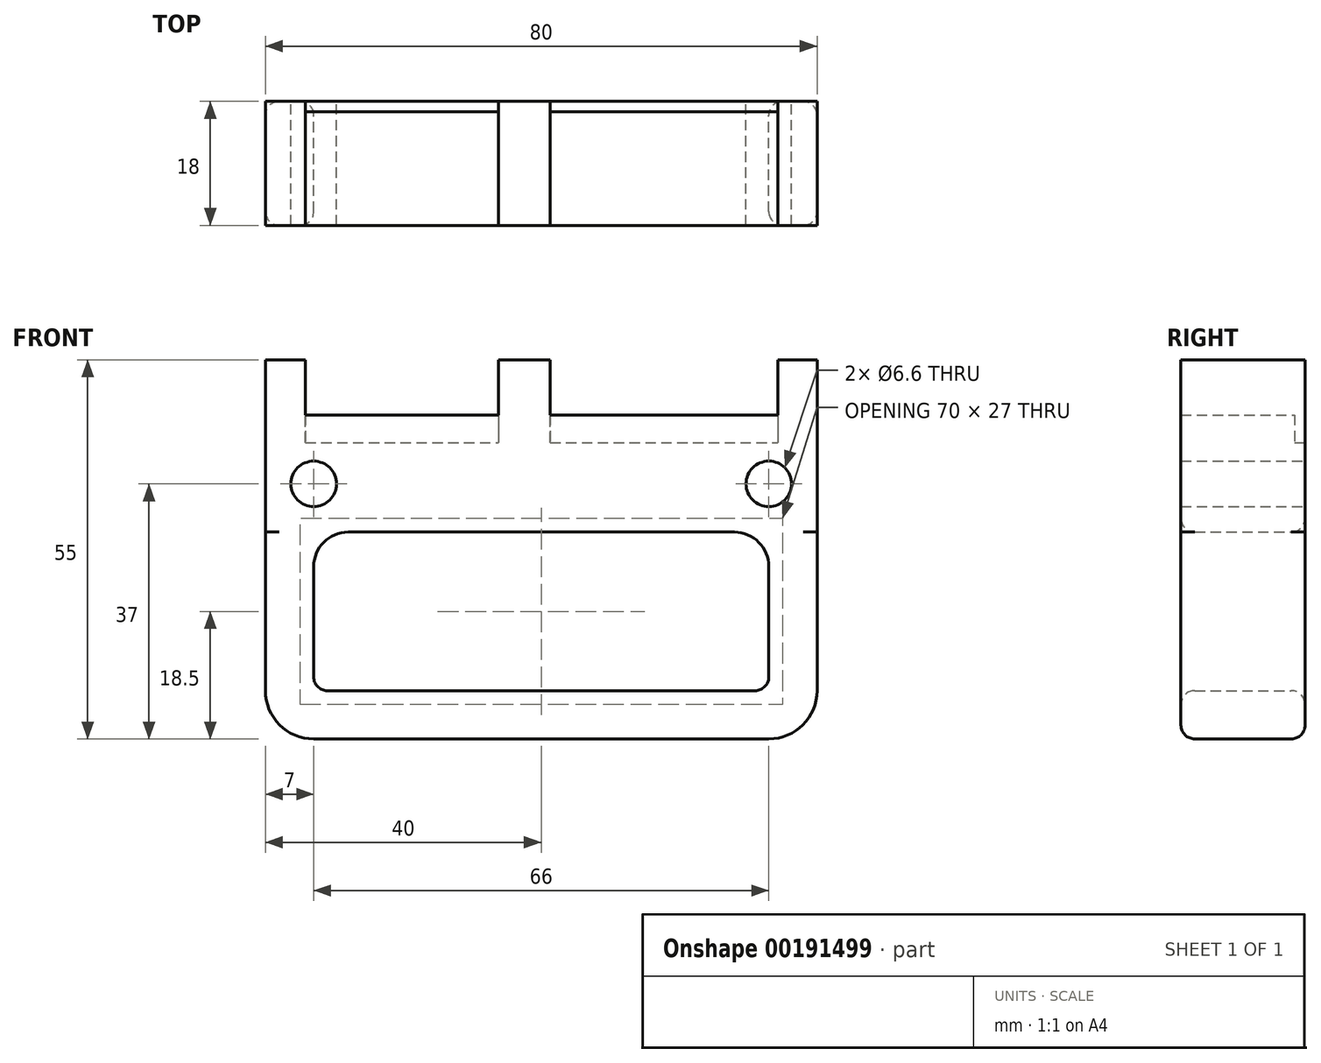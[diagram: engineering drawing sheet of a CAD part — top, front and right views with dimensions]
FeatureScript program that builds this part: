
annotation { "Feature Type Name" : "Feature", "Feature Type Description" : "" }
export const myFeature = defineFeature(function(context is Context, id is Id, definition is map)
    precondition{}
    {
        {
            var Q0;
            Q0=qCreatedBy(makeId("Front.planeOp"),FACE);
            var sketch = newSketch(context, id + "F0", { "sketchPlane" : qUnion([Q0])});
            skLineSegment(sketch, "E0.left", {"start": v(0, 0) * mm, "end": v(0, 25) * mm});
            skLineSegment(sketch, "E0.right", {"start": v(80, 0) * mm, "end": v(80, 25) * mm});
            skLineSegment(sketch, "E1", {"start": v(80, 25) * mm, "end": v(74.3, 25) * mm});
            skLineSegment(sketch, "E2", {"start": v(74.3, 25) * mm, "end": v(74.3, 17) * mm});
            skLineSegment(sketch, "E3", {"start": v(74.3, 17) * mm, "end": v(41.3, 17) * mm});
            skLineSegment(sketch, "E4", {"start": v(41.3, 17) * mm, "end": v(41.3, 25) * mm});
            skLineSegment(sketch, "E5", {"start": v(41.3, 25) * mm, "end": v(33.8, 25) * mm});
            skLineSegment(sketch, "E6", {"start": v(33.8, 25) * mm, "end": v(33.8, 17) * mm});
            skLineSegment(sketch, "E7", {"start": v(33.8, 17) * mm, "end": v(5.8, 17) * mm});
            skLineSegment(sketch, "E8", {"start": v(5.8, 17) * mm, "end": v(5.8, 25) * mm});
            skLineSegment(sketch, "E9", {"start": v(5.8, 25) * mm, "end": v(0, 25) * mm});
            skLineSegment(sketch, "E10.top", {"start": v(0, 7) * mm, "end": v(7, 7) * mm, "construction": true});
            skLineSegment(sketch, "E10.left", {"start": v(0, 0) * mm, "end": v(0, 7) * mm, "construction": true});
            skLineSegment(sketch, "E10.right", {"start": v(7, 0) * mm, "end": v(7, 7) * mm, "construction": true});
            skLineSegment(sketch, "E11.top", {"start": v(80, 7) * mm, "end": v(73, 7) * mm, "construction": true});
            skLineSegment(sketch, "E11.left", {"start": v(80, 0) * mm, "end": v(80, 7) * mm, "construction": true});
            skLineSegment(sketch, "E11.right", {"start": v(73, 0) * mm, "end": v(73, 7) * mm, "construction": true});
            skCircle(sketch, "E12", {"center": v(7, 7) * mm, "radius": 3.3 * mm});
            skCircle(sketch, "E13", {"center": v(73, 7) * mm, "radius": 3.3 * mm});
            skLineSegment(sketch, "E14.top", {"start": v(12, 0) * mm, "end": v(68, 0) * mm});
            skPoint(sketch, "E15.visualSharp", {"position": v(0, -30) * mm});
            skPoint(sketch, "E16.visualSharp", {"position": v(80, -30) * mm});
            skPoint(sketch, "E17.visualSharp", {"position": v(7, -23) * mm});
            skPoint(sketch, "E18.visualSharp", {"position": v(73, -23) * mm});
            skPoint(sketch, "E19.visualSharp", {"position": v(73, 0) * mm});
            skArc(sketch, "E19.filletArc", {"start": v(73, -5) * mm, "mid": v(71.54, -1.46) * mm, "end": v(68, 0) * mm});
            skPoint(sketch, "E20.visualSharp", {"position": v(7, 0) * mm});
            skArc(sketch, "E20.filletArc", {"start": v(12, 0) * mm, "mid": v(8.46, -1.46) * mm, "end": v(7, -5) * mm});
            skLineSegment(sketch, "E21", {"start": v(0, 0) * mm, "end": v(0, -23) * mm});
            skLineSegment(sketch, "E22", {"start": v(73, -30) * mm, "end": v(7, -30) * mm});
            skLineSegment(sketch, "E23", {"start": v(80, 0) * mm, "end": v(80, -23) * mm});
            skArc(sketch, "E24.filletArc", {"start": v(0, -23) * mm, "mid": v(2.05, -27.95) * mm, "end": v(7, -30) * mm});
            skArc(sketch, "E25.filletArc", {"start": v(73, -30) * mm, "mid": v(77.95, -27.95) * mm, "end": v(80, -23) * mm});
            skLineSegment(sketch, "E26.bottom", {"start": v(0, -30) * mm, "end": v(7, -30) * mm, "construction": true});
            skLineSegment(sketch, "E26.top", {"start": v(0, -23) * mm, "end": v(7, -23) * mm, "construction": true});
            skLineSegment(sketch, "E26.left", {"start": v(0, -30) * mm, "end": v(0, -23) * mm, "construction": true});
            skLineSegment(sketch, "E26.right", {"start": v(7, -30) * mm, "end": v(7, -23) * mm, "construction": true});
            skLineSegment(sketch, "E27.bottom", {"start": v(80, -30) * mm, "end": v(73, -30) * mm, "construction": true});
            skLineSegment(sketch, "E27.top", {"start": v(80, -23) * mm, "end": v(73, -23) * mm, "construction": true});
            skLineSegment(sketch, "E27.left", {"start": v(80, -30) * mm, "end": v(80, -23) * mm, "construction": true});
            skLineSegment(sketch, "E27.right", {"start": v(73, -30) * mm, "end": v(73, -23) * mm, "construction": true});
            skLineSegment(sketch, "E28", {"start": v(7, -5) * mm, "end": v(7, -21) * mm});
            skLineSegment(sketch, "E29", {"start": v(9, -23) * mm, "end": v(71, -23) * mm});
            skLineSegment(sketch, "E30", {"start": v(73, -5) * mm, "end": v(73, -21) * mm});
            skArc(sketch, "E31.filletArc", {"start": v(7, -21) * mm, "mid": v(7.59, -22.41) * mm, "end": v(9, -23) * mm});
            skArc(sketch, "E32.filletArc", {"start": v(71, -23) * mm, "mid": v(72.41, -22.41) * mm, "end": v(73, -21) * mm});
            skSolve(sketch);
        }
        {
            var Q0;
            Q0=makeQuery(id+"F0.imprint","IMPRINT",FACE,{"disambiguationData":[TD([[makeQuery(id+"F0.imprint","IMPRINT",EDGE,{"derivedFrom":sQuery(id+"F0.wireOp",EDGE,"E0.left")}),-1.0]])]});
            extrude(context, id + "F1", {"entities" : qUnion([Q0]), "depth" : 18 * mm});
        }
        {
            var Q0;
            Q0=makeQuery(id+"F1.opExtrude","CAP_FACE",FACE,{"disambiguationData":[OSD([sQuery(id+"F0.wireOp",EDGE,"E0.bottom"),sQuery(id+"F0.wireOp",EDGE,"E0.left"),sQuery(id+"F0.wireOp",EDGE,"E0.right"),sQuery(id+"F0.wireOp",EDGE,"E1"),sQuery(id+"F0.wireOp",EDGE,"E2"),sQuery(id+"F0.wireOp",EDGE,"E3"),sQuery(id+"F0.wireOp",EDGE,"E4"),sQuery(id+"F0.wireOp",EDGE,"E5"),sQuery(id+"F0.wireOp",EDGE,"E6"),sQuery(id+"F0.wireOp",EDGE,"E7"),sQuery(id+"F0.wireOp",EDGE,"E8"),sQuery(id+"F0.wireOp",EDGE,"E9"),sQuery(id+"F0.wireOp",EDGE,"E12"),sQuery(id+"F0.wireOp",EDGE,"E13"),sQuery(id+"F0.wireOp",EDGE,"ocKFlsXm-vWDa-OrpV-uGXT-8O8tEcb7mLHl.top"),sQuery(id+"F0.wireOp",EDGE,"ocKFlsXm-vWDa-OrpV-uGXT-8O8tEcb7mLHl.left"),sQuery(id+"F0.wireOp",EDGE,"ocKFlsXm-vWDa-OrpV-uGXT-8O8tEcb7mLHl.right"),sQuery(id+"F0.wireOp",EDGE,"41f4592c-d5e8-44ce-ae2d-2787e6d9c6fd.trimOffspring")])],"isStart":true});
            var sketch = newSketch(context, id + "F2", { "sketchPlane" : qUnion([Q0])});
            skLineSegment(sketch, "E33.left", {"start": v(-74.3, 17) * mm, "end": v(-74.3, 13) * mm});
            skLineSegment(sketch, "E34.left", {"start": v(-33.8, 17) * mm, "end": v(-33.8, 13) * mm});
            skLineSegment(sketch, "E35.left", {"start": v(-41.3, 17) * mm, "end": v(-41.3, 13) * mm});
            skLineSegment(sketch, "E36", {"start": v(-74.3, 17) * mm, "end": v(-41.3, 17) * mm});
            skLineSegment(sketch, "E37", {"start": v(-41.3, 13) * mm, "end": v(-74.3, 13) * mm});
            skLineSegment(sketch, "E38", {"start": v(-33.8, 17) * mm, "end": v(-5.8, 17) * mm});
            skLineSegment(sketch, "E39", {"start": v(-5.8, 17) * mm, "end": v(-5.8, 13) * mm});
            skLineSegment(sketch, "E40", {"start": v(-5.8, 13) * mm, "end": v(-33.8, 13) * mm});
            skSolve(sketch);
        }
        {
            var Q0;
            Q0 = qSketchRegion(id + "F2", true);
            extrude(context, id + "F3", {"entities" : qUnion([Q0]), "operationType" : NewBodyOperationType.REMOVE, "oppositeDirection" : true, "depth" : 1.5 * mm});
        }
        {
            var Q0;
            Q0=makeQuery(id+"F1.opExtrude","CAP_EDGE",EDGE,{"disambiguationData":[OSD([sQuery(id+"F0.wireOp",EDGE,"E32.filletArc")])],"isStart":true});
            var Q1;
            Q1=makeQuery(id+"F1.opExtrude","CAP_EDGE",EDGE,{"disambiguationData":[OSD([sQuery(id+"F0.wireOp",EDGE,"E30")])],"isStart":true});
            var Q2;
            Q2=makeQuery(id+"F1.opExtrude","CAP_EDGE",EDGE,{"disambiguationData":[OSD([sQuery(id+"F0.wireOp",EDGE,"E28")])],"isStart":false});
            var Q3;
            Q3=makeQuery(id+"F1.opExtrude","CAP_EDGE",EDGE,{"disambiguationData":[OSD([sQuery(id+"F0.wireOp",EDGE,"E22")])],"isStart":true});
            var Q4;
            Q4=makeQuery(id+"F1.opExtrude","CAP_EDGE",EDGE,{"disambiguationData":[OSD([sQuery(id+"F0.wireOp",EDGE,"E0.left"),sQuery(id+"F0.wireOp",EDGE,"E21")])],"isStart":false});
            fillet(context, id + "F4", {"entities" : qUnion([Q0, Q1, Q2, Q3, Q4]), "radius" : 2 * mm, "tangentPropagation" : true, "allowEdgeOverflow" : false});
        }
        {
            var Q0;
            Q0=makeQuery(id+"F1.opExtrude","SWEPT_FACE",FACE,{"disambiguationData":[OSD([sQuery(id+"F0.wireOp",EDGE,"E9")])]});
            var sketch = newSketch(context, id + "F5", { "sketchPlane" : qUnion([Q0])});
            skLineSegment(sketch, "E41.bottom", {"start": v(5.8, 0) * mm, "end": v(0, 0) * mm});
            skLineSegment(sketch, "E41.top", {"start": v(5.8, -18) * mm, "end": v(0, -18) * mm});
            skLineSegment(sketch, "E41.left", {"start": v(5.8, 0) * mm, "end": v(5.8, -18) * mm});
            skLineSegment(sketch, "E41.right", {"start": v(0, 0) * mm, "end": v(0, -18) * mm});
            skLineSegment(sketch, "E42", {"start": v(5.8, 0) * mm, "end": v(74.3, 0) * mm, "construction": true});
            skLineSegment(sketch, "E43.bottom", {"start": v(74.3, 0) * mm, "end": v(80, 0) * mm});
            skLineSegment(sketch, "E43.top", {"start": v(74.3, -18) * mm, "end": v(80, -18) * mm});
            skLineSegment(sketch, "E43.left", {"start": v(74.3, 0) * mm, "end": v(74.3, -18) * mm});
            skLineSegment(sketch, "E43.right", {"start": v(80, 0) * mm, "end": v(80, -18) * mm});
            skSolve(sketch);
        }
        {
            var Q0;
            Q0 = qSketchRegion(id + "F5", true);
            extrude(context, id + "F6", {"entities" : qUnion([Q0]), "operationType" : NewBodyOperationType.ADD, "oppositeDirection" : true, "depth" : 25 * mm});
        }
        {
            var Q0;
            Q0=makeQuery(id+"F6.boolean.opBoolean","MERGE",FACE,{"derivedFrom":[makeQuery(id+"F1.opExtrude","CAP_FACE",FACE,{"disambiguationData":[OSD([sQuery(id+"F0.wireOp",EDGE,"E0.left"),sQuery(id+"F0.wireOp",EDGE,"E0.right"),sQuery(id+"F0.wireOp",EDGE,"E1"),sQuery(id+"F0.wireOp",EDGE,"E2"),sQuery(id+"F0.wireOp",EDGE,"E3"),sQuery(id+"F0.wireOp",EDGE,"E4"),sQuery(id+"F0.wireOp",EDGE,"E5"),sQuery(id+"F0.wireOp",EDGE,"E6"),sQuery(id+"F0.wireOp",EDGE,"E7"),sQuery(id+"F0.wireOp",EDGE,"E8"),sQuery(id+"F0.wireOp",EDGE,"E9"),sQuery(id+"F0.wireOp",EDGE,"E12"),sQuery(id+"F0.wireOp",EDGE,"E13"),sQuery(id+"F0.wireOp",EDGE,"E14.top"),sQuery(id+"F0.wireOp",EDGE,"E19.filletArc"),sQuery(id+"F0.wireOp",EDGE,"E20.filletArc"),sQuery(id+"F0.wireOp",EDGE,"E21"),sQuery(id+"F0.wireOp",EDGE,"E22"),sQuery(id+"F0.wireOp",EDGE,"E23"),sQuery(id+"F0.wireOp",EDGE,"E24.filletArc"),sQuery(id+"F0.wireOp",EDGE,"E25.filletArc"),sQuery(id+"F0.wireOp",EDGE,"E28"),sQuery(id+"F0.wireOp",EDGE,"E29"),sQuery(id+"F0.wireOp",EDGE,"E30"),sQuery(id+"F0.wireOp",EDGE,"E31.filletArc"),sQuery(id+"F0.wireOp",EDGE,"E32.filletArc")])],"isStart":false}),makeQuery(id+"F6.opExtrude","SWEPT_FACE",FACE,{"disambiguationData":[OSD([sQuery(id+"F5.wireOp",EDGE,"E41.top")])]}),makeQuery(id+"F6.opExtrude","SWEPT_FACE",FACE,{"disambiguationData":[OSD([sQuery(id+"F5.wireOp",EDGE,"E43.top")])]})]});
            var sketch = newSketch(context, id + "F7", { "sketchPlane" : qUnion([Q0])});
            skCircle(sketch, "E44", {"center": v(73, 7) * mm, "radius": 3.3 * mm});
            skCircle(sketch, "E45", {"center": v(7, 7) * mm, "radius": 3.3 * mm});
            skSolve(sketch);
        }
        {
            var Q0;
            Q0 = qSketchRegion(id + "F7", true);
            extrude(context, id + "F8", {"entities" : qUnion([Q0]), "operationType" : NewBodyOperationType.REMOVE, "endBound" : BoundingType.THROUGH_ALL, "oppositeDirection" : true, "depth" : 25 * mm});
        }
    });
